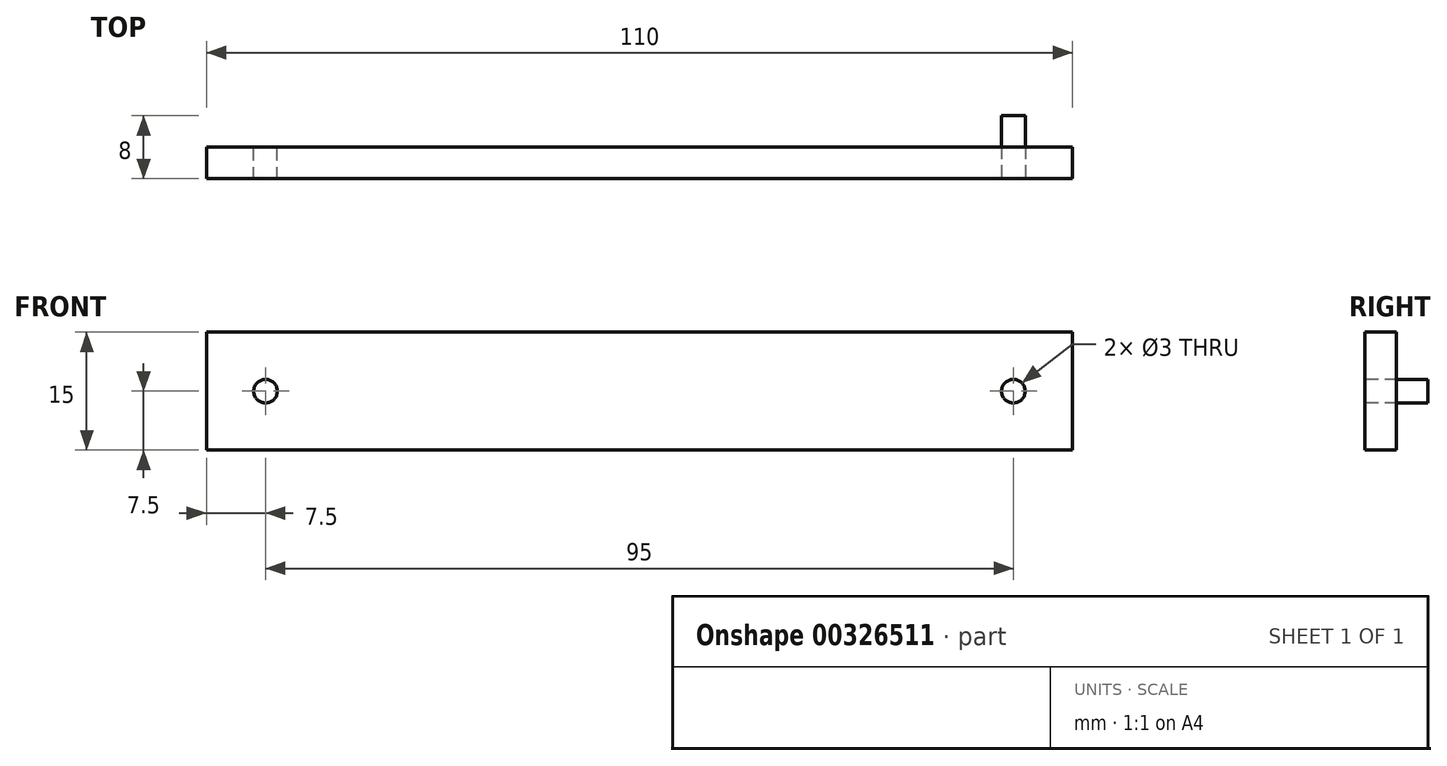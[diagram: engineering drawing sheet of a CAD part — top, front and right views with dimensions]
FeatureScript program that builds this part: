
annotation { "Feature Type Name" : "Feature", "Feature Type Description" : "" }
export const myFeature = defineFeature(function(context is Context, id is Id, definition is map)
    precondition{}
    {
        {
            var Q0;
            Q0=qCreatedBy(makeId("Front.planeOp"),FACE);
            var sketch = newSketch(context, id + "F0", { "sketchPlane" : qUnion([Q0])});
            skLineSegment(sketch, "E0", {"start": v(0, 0) * mm, "end": v(110, 0) * mm});
            skLineSegment(sketch, "E1", {"start": v(110, 0) * mm, "end": v(110, 15) * mm});
            skLineSegment(sketch, "E2", {"start": v(110, 15) * mm, "end": v(0, 15) * mm});
            skLineSegment(sketch, "E3", {"start": v(0, 15) * mm, "end": v(0, 0) * mm});
            skLineSegment(sketch, "E4", {"start": v(110, 7.5) * mm, "end": v(102.5, 7.5) * mm, "construction": true});
            skCircle(sketch, "E5", {"center": v(102.5, 7.5) * mm, "radius": 1.5 * mm});
            skLineSegment(sketch, "E6", {"start": v(0, 7.5) * mm, "end": v(7.5, 7.5) * mm, "construction": true});
            skCircle(sketch, "E7", {"center": v(7.5, 7.5) * mm, "radius": 1.5 * mm});
            skSolve(sketch);
        }
        {
            var Q0;
            Q0=makeQuery(id+"F0.imprint","IMPRINT",FACE,{"disambiguationData":[TD([[makeQuery(id+"F0.imprint","IMPRINT",EDGE,{"derivedFrom":sQuery(id+"F0.wireOp",EDGE,"E0")}),1.0]])]});
            extrude(context, id + "F1", {"entities" : qUnion([Q0]), "depth" : 4 * mm});
        }
        {
            var Q0;
            Q0=makeQuery(id+"F1.opExtrude","CAP_FACE",FACE,{"disambiguationData":[OSD([sQuery(id+"F0.wireOp",EDGE,"E0"),sQuery(id+"F0.wireOp",EDGE,"E1"),sQuery(id+"F0.wireOp",EDGE,"E2"),sQuery(id+"F0.wireOp",EDGE,"E3"),sQuery(id+"F0.wireOp",EDGE,"E5"),sQuery(id+"F0.wireOp",EDGE,"E7")])],"isStart":false});
            var sketch = newSketch(context, id + "F2", { "sketchPlane" : qUnion([Q0])});
            skCircle(sketch, "E8.0", {"center": v(102.5, 7.5) * mm, "radius": 1.5 * mm});
            skSolve(sketch);
        }
        {
            var Q0;
            Q0=makeQuery(id+"F2.imprint","IMPRINT",FACE,{"disambiguationData":[TD([[makeQuery(id+"F2.imprint","IMPRINT",EDGE,{"derivedFrom":sQuery(id+"F2.wireOp",EDGE,"E8.0")}),1.0]])]});
            extrude(context, id + "F3", {"entities" : qUnion([Q0]), "oppositeDirection" : true, "depth" : 8 * mm});
        }
    });
